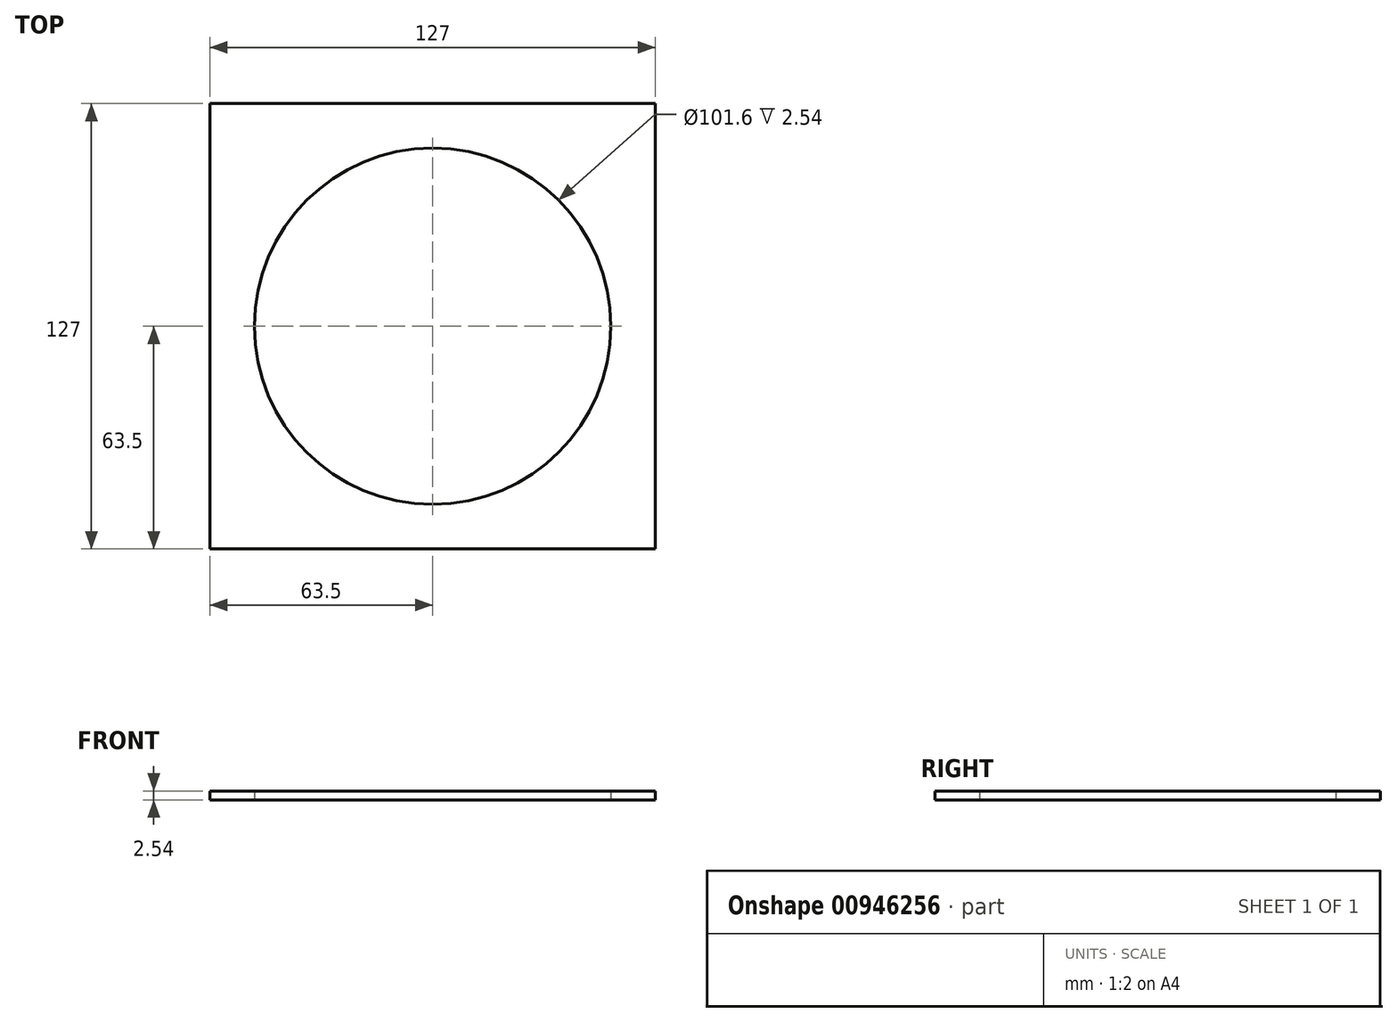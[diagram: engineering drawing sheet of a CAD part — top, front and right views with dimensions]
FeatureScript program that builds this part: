
annotation { "Feature Type Name" : "Feature", "Feature Type Description" : "" }
export const myFeature = defineFeature(function(context is Context, id is Id, definition is map)
    precondition{}
    {
        {
            var Q0;
            Q0=qCreatedBy(makeId("Top.planeOp"),FACE);
            var sketch = newSketch(context, id + "F0", { "sketchPlane" : qUnion([Q0])});
            skLineSegment(sketch, "E0.bottom", {"start": v(63.5, -63.5) * mm, "end": v(-63.5, -63.5) * mm});
            skLineSegment(sketch, "E0.top", {"start": v(63.5, 63.5) * mm, "end": v(-63.5, 63.5) * mm});
            skLineSegment(sketch, "E0.left", {"start": v(63.5, -63.5) * mm, "end": v(63.5, 63.5) * mm});
            skLineSegment(sketch, "E0.right", {"start": v(-63.5, -63.5) * mm, "end": v(-63.5, 63.5) * mm});
            skPoint(sketch, "E0.middle", {"position": v(0, 0) * mm});
            skSolve(sketch);
        }
        {
            var Q0;
            Q0=makeQuery(id+"F0.imprint","IMPRINT",FACE,{"disambiguationData":[TD([[makeQuery(id+"F0.imprint","IMPRINT",EDGE,{"derivedFrom":sQuery(id+"F0.wireOp",EDGE,"E0.bottom")}),-1.0]])]});
            extrude(context, id + "F1", {"entities" : qUnion([Q0]), "depth" : 2.54 * mm, "offsetDistance" : 25.4 * mm});
        }
        {
            var Q0;
            Q0=makeQuery(id+"F1.opExtrude","CAP_FACE",FACE,{"disambiguationData":[OSD([sQuery(id+"F0.wireOp",EDGE,"E0.bottom"),sQuery(id+"F0.wireOp",EDGE,"E0.top"),sQuery(id+"F0.wireOp",EDGE,"E0.left"),sQuery(id+"F0.wireOp",EDGE,"E0.right")])],"isStart":false});
            var sketch = newSketch(context, id + "F2", { "sketchPlane" : qUnion([Q0])});
            skLineSegment(sketch, "E1.bottom", {"start": v(-63.5, -63.5) * mm, "end": v(63.5, -63.5) * mm});
            skLineSegment(sketch, "E1.top", {"start": v(-63.5, 63.5) * mm, "end": v(63.5, 63.5) * mm});
            skLineSegment(sketch, "E1.left", {"start": v(-63.5, -63.5) * mm, "end": v(-63.5, 63.5) * mm});
            skLineSegment(sketch, "E1.right", {"start": v(63.5, -63.5) * mm, "end": v(63.5, 63.5) * mm});
            skPoint(sketch, "E1.middle", {"position": v(0, 0) * mm});
            skLineSegment(sketch, "E2.bottom", {"start": v(-62.23, -62.23) * mm, "end": v(62.23, -62.23) * mm});
            skLineSegment(sketch, "E2.top", {"start": v(-62.23, 62.23) * mm, "end": v(62.23, 62.23) * mm});
            skLineSegment(sketch, "E2.left", {"start": v(-62.23, -62.23) * mm, "end": v(-62.23, 62.23) * mm});
            skLineSegment(sketch, "E2.right", {"start": v(62.23, -62.23) * mm, "end": v(62.23, 62.23) * mm});
            skSolve(sketch);
        }
        {
            var Q0;
            Q0=sQuery(id+"F2.wireOp",EDGE,"E2.bottom");
            var Q1;
            Q1=sQuery(id+"F2.wireOp",EDGE,"E1.bottom");
            var Q2;
            Q2=sQuery(id+"F2.wireOp",EDGE,"E1.right");
            var Q3;
            Q3=sQuery(id+"F2.wireOp",EDGE,"E2.right");
            var Q4;
            Q4=sQuery(id+"F2.wireOp",EDGE,"E1.top");
            var Q5;
            Q5=sQuery(id+"F2.wireOp",EDGE,"E2.top");
            var Q6;
            Q6=sQuery(id+"F2.wireOp",EDGE,"E1.left");
            var Q7;
            Q7=sQuery(id+"F2.wireOp",EDGE,"E2.left");
            extrude(context, id + "F3", {"bodyType" : ToolBodyType.SURFACE, "surfaceEntities" : qUnion([Q0, Q1, Q2, Q3, Q4, Q5, Q6, Q7]), "depth" : 121.92 * mm, "offsetDistance" : 25.4 * mm});
        }
        {
            var Q0;
            Q0=sQuery(id+"F0.wireOp",VERTEX,"E0.middle");
            var Q1;
            Q1=makeQuery(id+"F1.opExtrude","SWEPT_BODY",BODY,{"disambiguationData":[OSD([sQuery(id+"F0.wireOp",EDGE,"E0.bottom"),sQuery(id+"F0.wireOp",EDGE,"E0.top"),sQuery(id+"F0.wireOp",EDGE,"E0.left"),sQuery(id+"F0.wireOp",EDGE,"E0.right")])]});
            hole(context, id + "F4", {"style" : HoleStyle.SIMPLE, "endStyle" : HoleEndStyle.THROUGH, "oppositeDirection" : true, "holeDiameter" : 101.6 * mm, "majorDiameter" : 6.35 * mm, "isTappedThrough" : true, "tappedDepth" : 12.7 * mm, "tapClearance" : 3, "locations" : qUnion([Q0]), "scope" : qUnion([Q1])});
        }
    });
